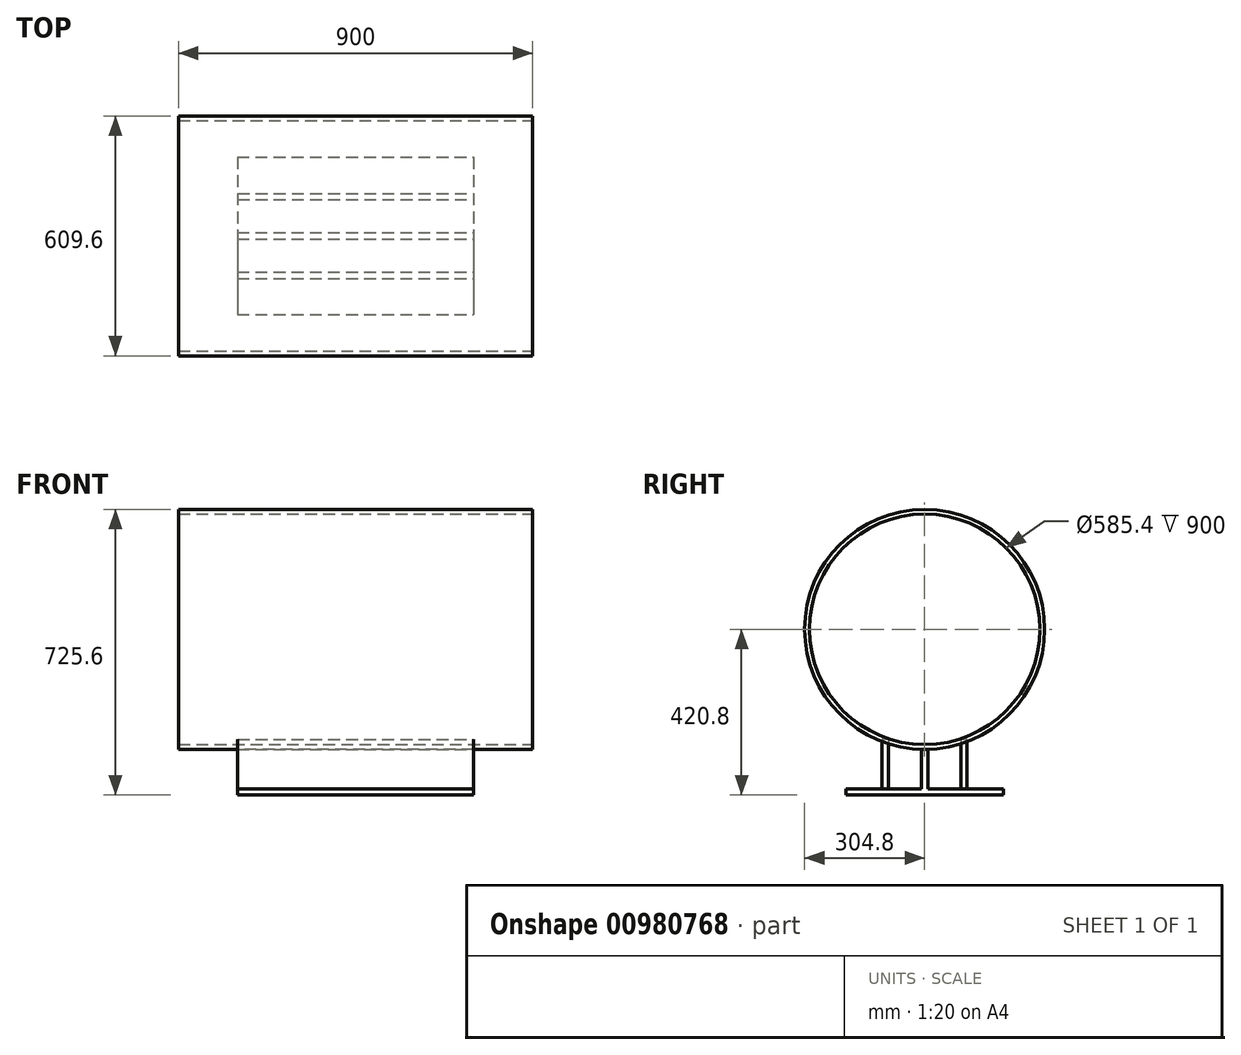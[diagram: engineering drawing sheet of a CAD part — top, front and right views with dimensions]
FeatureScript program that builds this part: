
annotation { "Feature Type Name" : "Feature", "Feature Type Description" : "" }
export const myFeature = defineFeature(function(context is Context, id is Id, definition is map)
    precondition{}
    {
        {
            var Q0;
            Q0=qCreatedBy(makeId("Top.planeOp"),FACE);
            var sketch = newSketch(context, id + "F0", { "sketchPlane" : qUnion([Q0])});
            skLineSegment(sketch, "E0.bottom", {"start": v(-300, 200) * mm, "end": v(300, 200) * mm});
            skLineSegment(sketch, "E0.top", {"start": v(-300, -200) * mm, "end": v(300, -200) * mm});
            skLineSegment(sketch, "E0.left", {"start": v(-300, 200) * mm, "end": v(-300, -200) * mm});
            skLineSegment(sketch, "E0.right", {"start": v(300, 200) * mm, "end": v(300, -200) * mm});
            skLineSegment(sketch, "E1", {"start": v(0, 200) * mm, "end": v(0, 0) * mm});
            skSolve(sketch);
        }
        {
            var Q0;
            Q0=makeQuery(id+"F0.imprint","IMPRINT",FACE,{"disambiguationData":[TD([[makeQuery(id+"F0.imprint","IMPRINT",EDGE,{"derivedFrom":sQuery(id+"F0.wireOp",EDGE,"E0.top")}),1.0]])]});
            extrude(context, id + "F1", {"entities" : qUnion([Q0]), "depth" : 16 * mm, "offsetDistance" : 25 * mm});
        }
        {
            var Q0;
            Q0=makeQuery(id+"F1.opExtrude","CAP_FACE",FACE,{"disambiguationData":[OSD([sQuery(id+"F0.wireOp",EDGE,"E0.bottom"),sQuery(id+"F0.wireOp",EDGE,"E0.top"),sQuery(id+"F0.wireOp",EDGE,"E0.left"),sQuery(id+"F0.wireOp",EDGE,"E0.right")])],"isStart":false});
            var sketch = newSketch(context, id + "F2", { "sketchPlane" : qUnion([Q0])});
            skLineSegment(sketch, "E2.bottom", {"start": v(-300, 8) * mm, "end": v(300, 8) * mm});
            skLineSegment(sketch, "E2.top", {"start": v(-300, -8) * mm, "end": v(300, -8) * mm});
            skLineSegment(sketch, "E2.left", {"start": v(-300, 8) * mm, "end": v(-300, -8) * mm});
            skLineSegment(sketch, "E2.right", {"start": v(300, 8) * mm, "end": v(300, -8) * mm});
            skSolve(sketch);
        }
        {
            var Q0;
            Q0=makeQuery(id+"F2.imprint","IMPRINT",FACE,{"disambiguationData":[TD([[makeQuery(id+"F2.imprint","IMPRINT",EDGE,{"derivedFrom":sQuery(id+"F2.wireOp",EDGE,"E2.bottom")}),-1.0]])]});
            var sketch = newSketch(context, id + "F3", { "sketchPlane" : qUnion([Q0])});
            skLineSegment(sketch, "E3.bottom", {"start": v(-299.48, 108) * mm, "end": v(300.52, 108) * mm});
            skLineSegment(sketch, "E3.top", {"start": v(-299.48, 92) * mm, "end": v(300.52, 92) * mm});
            skLineSegment(sketch, "E3.left", {"start": v(-299.48, 108) * mm, "end": v(-299.48, 92) * mm});
            skLineSegment(sketch, "E3.right", {"start": v(300.52, 108) * mm, "end": v(300.52, 92) * mm});
            skSolve(sketch);
        }
        {
            var Q0;
            Q0=makeQuery(id+"F2.imprint","IMPRINT",FACE,{"disambiguationData":[TD([[makeQuery(id+"F2.imprint","IMPRINT",EDGE,{"derivedFrom":sQuery(id+"F2.wireOp",EDGE,"E2.bottom")}),-1.0]])]});
            extrude(context, id + "F4", {"entities" : qUnion([Q0]), "operationType" : NewBodyOperationType.ADD, "depth" : 100 * mm, "offsetDistance" : 25 * mm});
        }
        {
            var Q0;
            Q0=qCreatedBy(makeId("Right.planeOp"),FACE);
            var sketch = newSketch(context, id + "F5", { "sketchPlane" : qUnion([Q0])});
            skCircle(sketch, "E4", {"center": v(0, 420.8) * mm, "radius": 304.8 * mm});
            skSolve(sketch);
        }
        {
            var Q0;
            Q0=makeQuery(id+"F5.imprint","IMPRINT",FACE,{"disambiguationData":[TD([[makeQuery(id+"F5.imprint","IMPRINT",EDGE,{"derivedFrom":sQuery(id+"F5.wireOp",EDGE,"E4")}),1.0]])]});
            extrude(context, id + "F6", {"entities" : qUnion([Q0]), "operationType" : NewBodyOperationType.ADD, "endBound" : BoundingType.SYMMETRIC, "depth" : 900 * mm, "offsetDistance" : 25 * mm});
        }
        {
            var Q0;
            Q0=makeQuery(id+"F6.opExtrude","CAP_FACE",FACE,{"disambiguationData":[OSD([sQuery(id+"F5.wireOp",EDGE,"E4")])],"isStart":false});
            var sketch = newSketch(context, id + "F7", { "sketchPlane" : qUnion([Q0])});
            skCircle(sketch, "E5", {"center": v(0, 420.8) * mm, "radius": 292.7 * mm});
            skSolve(sketch);
        }
        {
            var Q0;
            Q0=makeQuery(id+"F7.imprint","IMPRINT",FACE,{"disambiguationData":[TD([[makeQuery(id+"F7.imprint","IMPRINT",EDGE,{"derivedFrom":sQuery(id+"F7.wireOp",EDGE,"E5")}),1.0]])]});
            extrude(context, id + "F8", {"entities" : qUnion([Q0]), "operationType" : NewBodyOperationType.REMOVE, "endBound" : BoundingType.THROUGH_ALL, "oppositeDirection" : true, "depth" : 25 * mm, "offsetDistance" : 25 * mm});
        }
        {
            var Q0;
            {var subQ0=sQuery(id+"F0.wireOp",EDGE,"E0.right");var subQ1=sQuery(id+"F0.wireOp",EDGE,"E0.left");var subQ2=sQuery(id+"F0.wireOp",EDGE,"E0.top");Q0=makeQuery(id+"F4.boolean.opBoolean","SPLIT",FACE,{"disambiguationData":[TD([makeQuery(id+"F1.opExtrude","SWEPT_FACE",FACE,{"disambiguationData":[OSD([subQ2])]})])],"derivedFrom":makeQuery(id+"F1.opExtrude","CAP_FACE",FACE,{"disambiguationData":[OSD([sQuery(id+"F0.wireOp",EDGE,"E0.bottom"),subQ2,subQ1,subQ0])],"isStart":false})});}
            var sketch = newSketch(context, id + "F9", { "sketchPlane" : qUnion([Q0])});
            skLineSegment(sketch, "E6.bottom", {"start": v(-300, -92) * mm, "end": v(300, -92) * mm});
            skLineSegment(sketch, "E6.top", {"start": v(-300, -108) * mm, "end": v(300, -108) * mm});
            skLineSegment(sketch, "E6.left", {"start": v(-300, -92) * mm, "end": v(-300, -108) * mm});
            skLineSegment(sketch, "E6.right", {"start": v(300, -92) * mm, "end": v(300, -108) * mm});
            skSolve(sketch);
        }
        {
            var Q0;
            Q0=makeQuery(id+"F9.imprint","IMPRINT",FACE,{"disambiguationData":[TD([[makeQuery(id+"F9.imprint","IMPRINT",EDGE,{"derivedFrom":sQuery(id+"F9.wireOp",EDGE,"E6.bottom")}),-1.0]])]});
            extrude(context, id + "F10", {"entities" : qUnion([Q0]), "depth" : 125 * mm, "offsetDistance" : 25 * mm});
        }
        {
            var Q0;
            Q0=makeQuery(id+"F3.imprint","IMPRINT",FACE,{"disambiguationData":[TD([[makeQuery(id+"F3.imprint","IMPRINT",EDGE,{"derivedFrom":sQuery(id+"F3.wireOp",EDGE,"E3.bottom")}),-1.0]])]});
            extrude(context, id + "F11", {"entities" : qUnion([Q0]), "depth" : 125 * mm, "offsetDistance" : 25 * mm});
        }
    });
